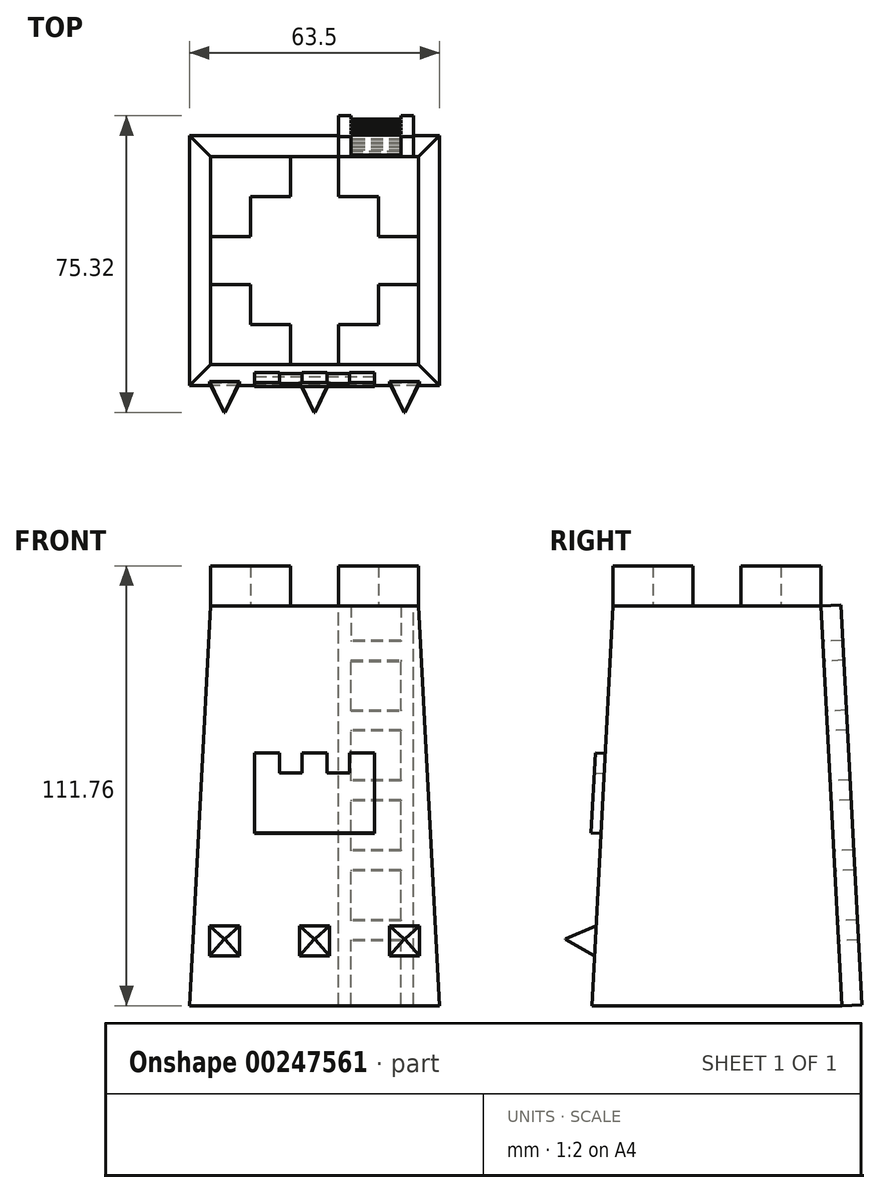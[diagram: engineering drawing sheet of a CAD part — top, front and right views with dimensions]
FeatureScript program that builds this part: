
annotation { "Feature Type Name" : "Feature", "Feature Type Description" : "" }
export const myFeature = defineFeature(function(context is Context, id is Id, definition is map)
    precondition{}
    {
        {
            var Q0;
            Q0=qCreatedBy(makeId("Top.planeOp"),FACE);
            var sketch = newSketch(context, id + "F0", { "sketchPlane" : qUnion([Q0])});
            skLineSegment(sketch, "E0.bottom", {"start": v(-28.1, 22.33) * mm, "end": v(35.4, 22.33) * mm});
            skLineSegment(sketch, "E0.top", {"start": v(-28.1, -41.17) * mm, "end": v(35.4, -41.17) * mm});
            skLineSegment(sketch, "E0.left", {"start": v(-28.1, 22.33) * mm, "end": v(-28.1, -41.17) * mm});
            skLineSegment(sketch, "E0.right", {"start": v(35.4, 22.33) * mm, "end": v(35.4, -41.17) * mm});
            skSolve(sketch);
        }
        {
            var Q0;
            Q0 = qSketchRegion(id + "F0", true);
            extrude(context, id + "F1", {"entities" : qUnion([Q0]), "depth" : 101.6 * mm, "hasDraft" : true, "draftAngle" : 3 * degree, "draftPullDirection" : true});
        }
        {
            var Q0;
            Q0=makeQuery(id+"F1.opExtrude","CAP_FACE",FACE,{"disambiguationData":[OSD([sQuery(id+"F0.wireOp",EDGE,"E0.bottom"),sQuery(id+"F0.wireOp",EDGE,"E0.top"),sQuery(id+"F0.wireOp",EDGE,"E0.left"),sQuery(id+"F0.wireOp",EDGE,"E0.right")])],"isStart":false});
            var sketch = newSketch(context, id + "F2", { "sketchPlane" : qUnion([Q0])});
            skLineSegment(sketch, "E1.bottom", {"start": v(-22.77, -15.52) * mm, "end": v(-12.6, -15.52) * mm});
            skLineSegment(sketch, "E1.top", {"start": v(-22.77, -35.84) * mm, "end": v(-12.6, -35.84) * mm});
            skLineSegment(sketch, "E1.left", {"start": v(-22.77, -15.52) * mm, "end": v(-22.77, -35.84) * mm});
            skLineSegment(sketch, "E1.right", {"start": v(-12.6, -15.52) * mm, "end": v(-12.6, -25.68) * mm});
            skLineSegment(sketch, "E2.bottom", {"start": v(-12.6, -25.68) * mm, "end": v(-2.45, -25.68) * mm});
            skLineSegment(sketch, "E2.top", {"start": v(-12.6, -35.84) * mm, "end": v(-2.45, -35.84) * mm});
            skLineSegment(sketch, "E2.right", {"start": v(-2.45, -25.68) * mm, "end": v(-2.45, -35.84) * mm});
            skLineSegment(sketch, "E3.bottom", {"start": v(30.08, -35.84) * mm, "end": v(19.92, -35.84) * mm});
            skLineSegment(sketch, "E3.top", {"start": v(30.08, -15.52) * mm, "end": v(19.92, -15.52) * mm});
            skLineSegment(sketch, "E3.left", {"start": v(30.08, -35.84) * mm, "end": v(30.08, -15.52) * mm});
            skLineSegment(sketch, "E3.right", {"start": v(19.92, -25.68) * mm, "end": v(19.92, -15.52) * mm});
            skLineSegment(sketch, "E4.bottom", {"start": v(19.92, -25.68) * mm, "end": v(9.76, -25.68) * mm});
            skLineSegment(sketch, "E4.top", {"start": v(19.92, -35.84) * mm, "end": v(9.76, -35.84) * mm});
            skLineSegment(sketch, "E4.right", {"start": v(9.76, -25.68) * mm, "end": v(9.76, -35.84) * mm});
            skLineSegment(sketch, "E5.bottom", {"start": v(-22.77, 17) * mm, "end": v(-12.6, 17) * mm});
            skLineSegment(sketch, "E5.top", {"start": v(-22.77, -3.31) * mm, "end": v(-12.6, -3.31) * mm});
            skLineSegment(sketch, "E5.left", {"start": v(-22.77, 17) * mm, "end": v(-22.77, -3.31) * mm});
            skLineSegment(sketch, "E5.right", {"start": v(-12.6, 6.85) * mm, "end": v(-12.6, -3.31) * mm});
            skLineSegment(sketch, "E6.bottom", {"start": v(-12.6, 17) * mm, "end": v(-2.45, 17) * mm});
            skLineSegment(sketch, "E6.top", {"start": v(-12.6, 6.85) * mm, "end": v(-2.45, 6.85) * mm});
            skLineSegment(sketch, "E6.right", {"start": v(-2.45, 17) * mm, "end": v(-2.45, 6.85) * mm});
            skLineSegment(sketch, "E7.bottom", {"start": v(30.08, 17) * mm, "end": v(19.92, 17) * mm});
            skLineSegment(sketch, "E7.top", {"start": v(30.08, -3.31) * mm, "end": v(19.92, -3.31) * mm});
            skLineSegment(sketch, "E7.left", {"start": v(30.08, 17) * mm, "end": v(30.08, -3.31) * mm});
            skLineSegment(sketch, "E7.right", {"start": v(19.92, 6.85) * mm, "end": v(19.92, -3.31) * mm});
            skLineSegment(sketch, "E8.bottom", {"start": v(19.92, 17) * mm, "end": v(9.76, 17) * mm});
            skLineSegment(sketch, "E8.top", {"start": v(19.92, 6.85) * mm, "end": v(9.76, 6.85) * mm});
            skLineSegment(sketch, "E8.right", {"start": v(9.76, 17) * mm, "end": v(9.76, 6.85) * mm});
            skSolve(sketch);
        }
        {
            var Q0;
            Q0 = qSketchRegion(id + "F2", true);
            extrude(context, id + "F3", {"entities" : qUnion([Q0]), "operationType" : NewBodyOperationType.ADD, "depth" : 10.16 * mm});
        }
        {
            var Q0;
            Q0=makeQuery(id+"F1.opExtrude","SWEPT_FACE",FACE,{"disambiguationData":[OSD([sQuery(id+"F0.wireOp",EDGE,"E0.top")])]});
            var sketch = newSketch(context, id + "F4", { "sketchPlane" : qUnion([Q0])});
            skLineSegment(sketch, "E9.bottom", {"start": v(-23.01, 18.17) * mm, "end": v(-15.4, 18.17) * mm});
            skLineSegment(sketch, "E9.top", {"start": v(-23.01, 10.55) * mm, "end": v(-15.4, 10.55) * mm});
            skLineSegment(sketch, "E9.left", {"start": v(-23.01, 18.17) * mm, "end": v(-23.01, 10.55) * mm});
            skLineSegment(sketch, "E9.right", {"start": v(-15.4, 18.17) * mm, "end": v(-15.4, 10.55) * mm});
            skLineSegment(sketch, "E10.bottom", {"start": v(-0.15, 18.17) * mm, "end": v(7.47, 18.17) * mm});
            skLineSegment(sketch, "E10.top", {"start": v(-0.15, 10.55) * mm, "end": v(7.47, 10.55) * mm});
            skLineSegment(sketch, "E10.left", {"start": v(-0.15, 18.17) * mm, "end": v(-0.15, 10.55) * mm});
            skLineSegment(sketch, "E10.right", {"start": v(7.47, 18.17) * mm, "end": v(7.47, 10.55) * mm});
            skLineSegment(sketch, "E11.bottom", {"start": v(22.7, 18.17) * mm, "end": v(30.33, 18.17) * mm});
            skLineSegment(sketch, "E11.top", {"start": v(22.7, 10.55) * mm, "end": v(30.33, 10.55) * mm});
            skLineSegment(sketch, "E11.left", {"start": v(22.7, 18.17) * mm, "end": v(22.7, 10.55) * mm});
            skLineSegment(sketch, "E11.right", {"start": v(30.33, 18.17) * mm, "end": v(30.33, 10.55) * mm});
            skSolve(sketch);
        }
        {
            var Q0;
            Q0 = qSketchRegion(id + "F4", true);
            extrude(context, id + "F5", {"entities" : qUnion([Q0]), "operationType" : NewBodyOperationType.ADD, "depth" : 7.62 * mm, "hasDraft" : true, "draftAngle" : 26 * degree, "draftPullDirection" : true});
        }
        {
            var Q0;
            Q0=makeQuery(id+"F1.opExtrude","SWEPT_FACE",FACE,{"disambiguationData":[OSD([sQuery(id+"F0.wireOp",EDGE,"E0.top")])]});
            var sketch = newSketch(context, id + "F6", { "sketchPlane" : qUnion([Q0])});
            skLineSegment(sketch, "E12.bottom", {"start": v(-11.58, 41.72) * mm, "end": v(18.9, 41.72) * mm});
            skLineSegment(sketch, "E12.top", {"start": v(-5.23, 56.96) * mm, "end": v(0.48, 56.96) * mm});
            skLineSegment(sketch, "E12.left", {"start": v(-11.58, 41.72) * mm, "end": v(-11.58, 56.96) * mm});
            skLineSegment(sketch, "E12.right", {"start": v(18.9, 41.72) * mm, "end": v(18.9, 56.96) * mm});
            skLineSegment(sketch, "E13.top", {"start": v(-11.58, 62.04) * mm, "end": v(-5.23, 62.04) * mm});
            skLineSegment(sketch, "E13.left", {"start": v(-11.58, 56.96) * mm, "end": v(-11.58, 62.04) * mm});
            skLineSegment(sketch, "E13.right", {"start": v(-5.23, 56.96) * mm, "end": v(-5.23, 62.04) * mm});
            skLineSegment(sketch, "E14.top", {"start": v(6.83, 62.04) * mm, "end": v(0.48, 62.04) * mm});
            skLineSegment(sketch, "E14.left", {"start": v(6.83, 56.96) * mm, "end": v(6.83, 62.04) * mm});
            skLineSegment(sketch, "E14.right", {"start": v(0.48, 56.96) * mm, "end": v(0.48, 62.04) * mm});
            skLineSegment(sketch, "E15.top", {"start": v(12.55, 62.04) * mm, "end": v(18.9, 62.04) * mm});
            skLineSegment(sketch, "E15.left", {"start": v(12.55, 56.96) * mm, "end": v(12.55, 62.04) * mm});
            skLineSegment(sketch, "E15.right", {"start": v(18.9, 56.96) * mm, "end": v(18.9, 62.04) * mm});
            skLineSegment(sketch, "E16.trimOffspring", {"start": v(6.83, 56.96) * mm, "end": v(12.55, 56.96) * mm});
            skLineSegment(sketch, "E17.trimOffspring", {"start": v(18.9, 56.96) * mm, "end": v(18.9, 56.96) * mm});
            skSolve(sketch);
        }
        {
            var Q0;
            Q0=makeQuery(id+"F6.imprint","IMPRINT",FACE,{"disambiguationData":[TD([[makeQuery(id+"F6.imprint","IMPRINT",EDGE,{"derivedFrom":sQuery(id+"F6.wireOp",EDGE,"E12.bottom")}),1.0]])]});
            extrude(context, id + "F7", {"entities" : qUnion([Q0]), "operationType" : NewBodyOperationType.ADD, "depth" : 2.54 * mm});
        }
        {
            var Q0;
            Q0=makeQuery(id+"F1.opExtrude","SWEPT_FACE",FACE,{"disambiguationData":[OSD([sQuery(id+"F0.wireOp",EDGE,"E0.bottom")])]});
            var sketch = newSketch(context, id + "F8", { "sketchPlane" : qUnion([Q0])});
            skLineSegment(sketch, "E18.bottom", {"start": v(-28.81, -1.17) * mm, "end": v(-25.64, -1.17) * mm});
            skLineSegment(sketch, "E18.top", {"start": v(-28.81, 100.57) * mm, "end": v(-25.64, 100.57) * mm});
            skLineSegment(sketch, "E18.left", {"start": v(-28.81, -1.17) * mm, "end": v(-28.81, 100.57) * mm});
            skLineSegment(sketch, "E18.right", {"start": v(-9.76, -1.17) * mm, "end": v(-9.76, 100.57) * mm});
            skLineSegment(sketch, "E19.top", {"start": v(-25.64, 15.34) * mm, "end": v(-12.94, 15.34) * mm});
            skLineSegment(sketch, "E19.left", {"start": v(-25.64, -1.17) * mm, "end": v(-25.64, 15.34) * mm});
            skLineSegment(sketch, "E19.right", {"start": v(-12.94, -1.17) * mm, "end": v(-12.94, 15.34) * mm});
            skLineSegment(sketch, "E20.trimOffspring", {"start": v(-12.94, -1.17) * mm, "end": v(-9.76, -1.17) * mm});
            skLineSegment(sketch, "E21.bottom", {"start": v(-25.64, 20.42) * mm, "end": v(-12.94, 20.42) * mm});
            skLineSegment(sketch, "E21.top", {"start": v(-25.64, 33.12) * mm, "end": v(-12.94, 33.12) * mm});
            skLineSegment(sketch, "E21.left", {"start": v(-25.64, 20.42) * mm, "end": v(-25.64, 33.12) * mm});
            skLineSegment(sketch, "E21.right", {"start": v(-12.94, 20.42) * mm, "end": v(-12.94, 33.12) * mm});
            skLineSegment(sketch, "E22.bottom", {"start": v(-25.64, 38.2) * mm, "end": v(-12.94, 38.2) * mm});
            skLineSegment(sketch, "E22.top", {"start": v(-25.64, 50.9) * mm, "end": v(-12.94, 50.9) * mm});
            skLineSegment(sketch, "E22.left", {"start": v(-25.64, 38.2) * mm, "end": v(-25.64, 50.9) * mm});
            skLineSegment(sketch, "E22.right", {"start": v(-12.94, 38.2) * mm, "end": v(-12.94, 50.9) * mm});
            skLineSegment(sketch, "E23.bottom", {"start": v(-25.64, 55.98) * mm, "end": v(-12.94, 55.98) * mm});
            skLineSegment(sketch, "E23.top", {"start": v(-25.64, 68.68) * mm, "end": v(-12.94, 68.68) * mm});
            skLineSegment(sketch, "E23.left", {"start": v(-25.64, 55.98) * mm, "end": v(-25.64, 68.68) * mm});
            skLineSegment(sketch, "E23.right", {"start": v(-12.94, 55.98) * mm, "end": v(-12.94, 68.68) * mm});
            skLineSegment(sketch, "E24.bottom", {"start": v(-12.94, 73.76) * mm, "end": v(-25.64, 73.76) * mm});
            skLineSegment(sketch, "E24.top", {"start": v(-12.94, 86.46) * mm, "end": v(-25.64, 86.46) * mm});
            skLineSegment(sketch, "E24.left", {"start": v(-12.94, 73.76) * mm, "end": v(-12.94, 86.46) * mm});
            skLineSegment(sketch, "E24.right", {"start": v(-25.64, 73.76) * mm, "end": v(-25.64, 86.46) * mm});
            skLineSegment(sketch, "E25.top", {"start": v(-25.64, 91.54) * mm, "end": v(-12.94, 91.54) * mm});
            skLineSegment(sketch, "E25.left", {"start": v(-25.64, 100.57) * mm, "end": v(-25.64, 91.54) * mm});
            skLineSegment(sketch, "E25.right", {"start": v(-12.94, 100.57) * mm, "end": v(-12.94, 91.54) * mm});
            skLineSegment(sketch, "E26.trimOffspring", {"start": v(-12.94, 100.57) * mm, "end": v(-9.76, 100.57) * mm});
            skSolve(sketch);
        }
        {
            var Q0;
            Q0 = qSketchRegion(id + "F8", true);
            extrude(context, id + "F9", {"entities" : qUnion([Q0]), "operationType" : NewBodyOperationType.ADD, "depth" : 5.08 * mm});
        }
    });
